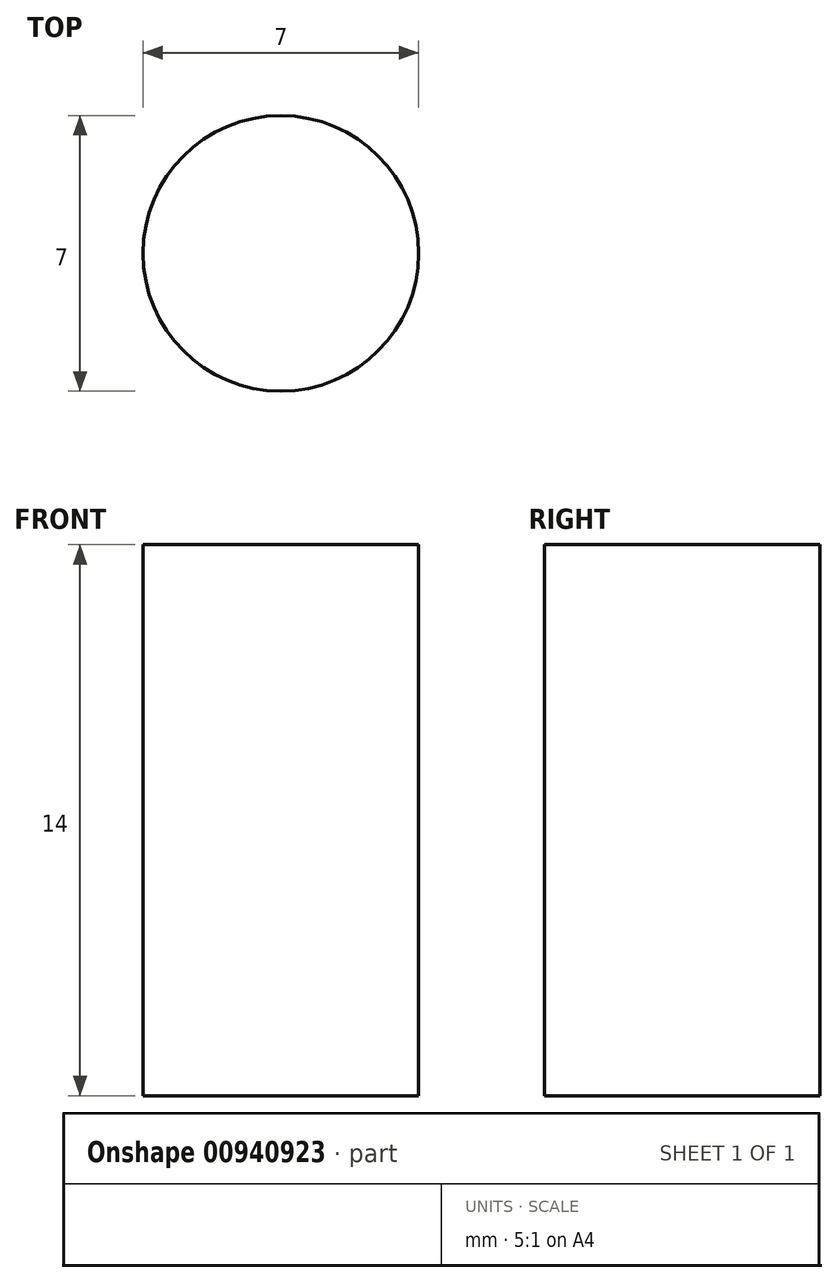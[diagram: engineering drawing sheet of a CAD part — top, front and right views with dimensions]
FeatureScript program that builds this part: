
annotation { "Feature Type Name" : "Feature", "Feature Type Description" : "" }
export const myFeature = defineFeature(function(context is Context, id is Id, definition is map)
    precondition{}
    {
        {
            var Q0;
            Q0=qCreatedBy(makeId("Top.planeOp"),FACE);
            var sketch = newSketch(context, id + "F0", { "sketchPlane" : qUnion([Q0])});
            skCircle(sketch, "E0", {"center": v(0, 0) * mm, "radius": 3.5 * mm});
            skSolve(sketch);
        }
        {
            var Q0;
            Q0 = qSketchRegion(id + "F0", true);
            extrude(context, id + "F1", {"entities" : qUnion([Q0]), "depth" : 14 * mm, "offsetDistance" : 25 * mm});
        }
    });
